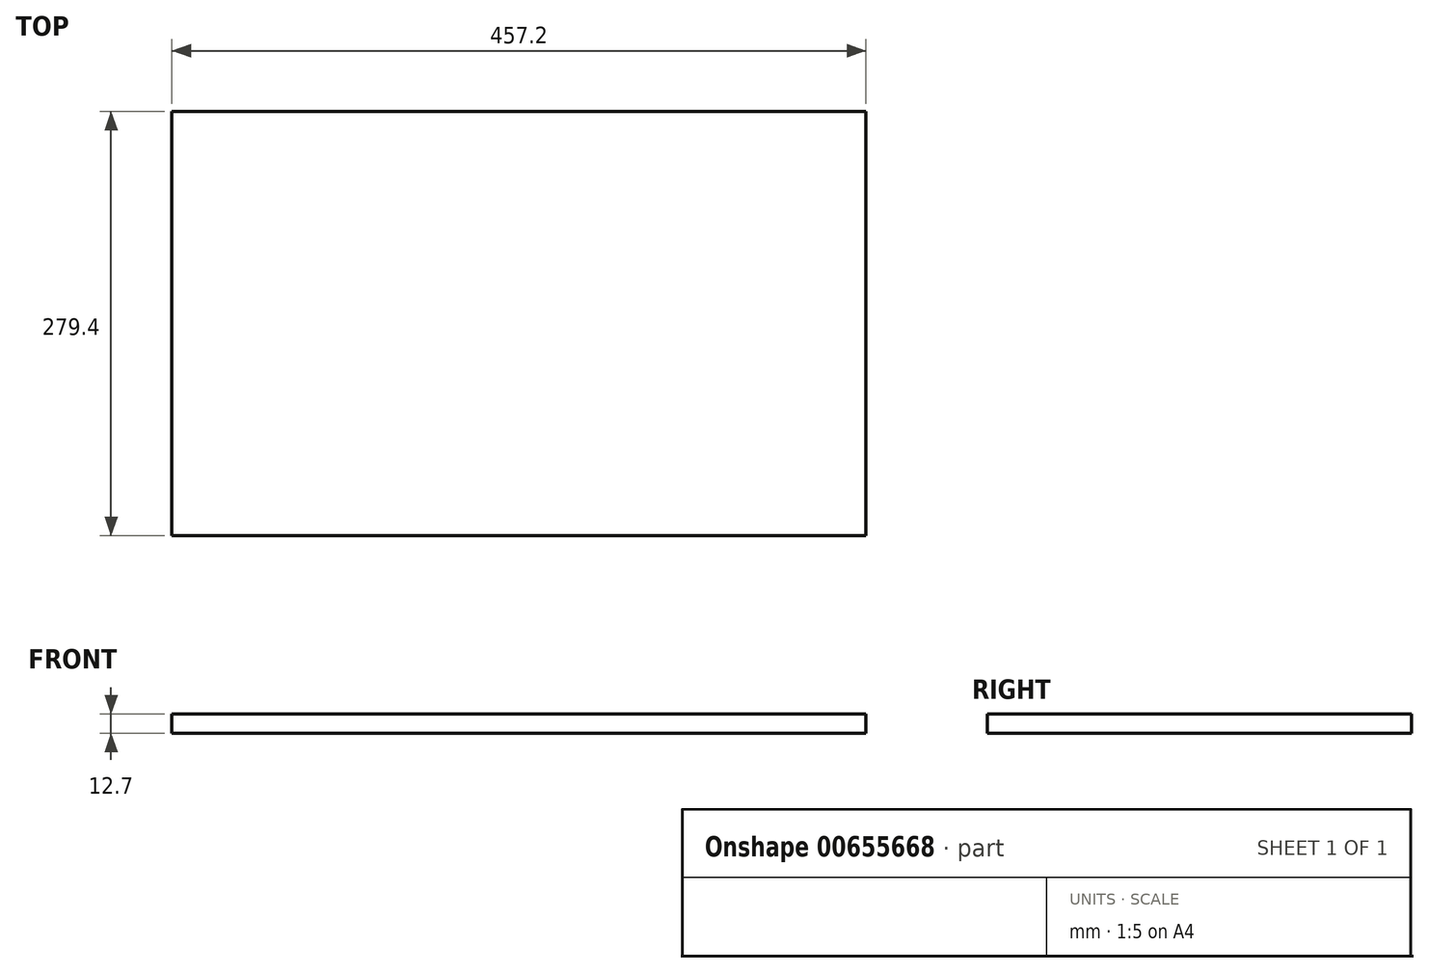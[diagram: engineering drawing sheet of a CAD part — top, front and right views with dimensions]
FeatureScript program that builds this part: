
annotation { "Feature Type Name" : "Feature", "Feature Type Description" : "" }
export const myFeature = defineFeature(function(context is Context, id is Id, definition is map)
    precondition{}
    {
        {
            var Q0;
            Q0=qCreatedBy(makeId("Top.planeOp"),FACE);
            var sketch = newSketch(context, id + "F0", { "sketchPlane" : qUnion([Q0])});
            skLineSegment(sketch, "E0.bottom", {"start": v(-231.66, 45.85) * mm, "end": v(225.54, 45.85) * mm});
            skLineSegment(sketch, "E0.top", {"start": v(-231.66, -233.55) * mm, "end": v(225.54, -233.55) * mm});
            skLineSegment(sketch, "E0.left", {"start": v(-231.66, 45.85) * mm, "end": v(-231.66, -233.55) * mm});
            skLineSegment(sketch, "E0.right", {"start": v(225.54, 45.85) * mm, "end": v(225.54, -233.55) * mm});
            skSolve(sketch);
        }
        {
            var Q0;
            Q0=makeQuery(id+"F0.imprint","IMPRINT",FACE,{"disambiguationData":[TD([[makeQuery(id+"F0.imprint","IMPRINT",EDGE,{"derivedFrom":sQuery(id+"F0.wireOp",EDGE,"E0.bottom")}),-1.0]])]});
            extrude(context, id + "F1", {"entities" : qUnion([Q0]), "depth" : 12.7 * mm, "offsetDistance" : 25.4 * mm});
        }
    });
